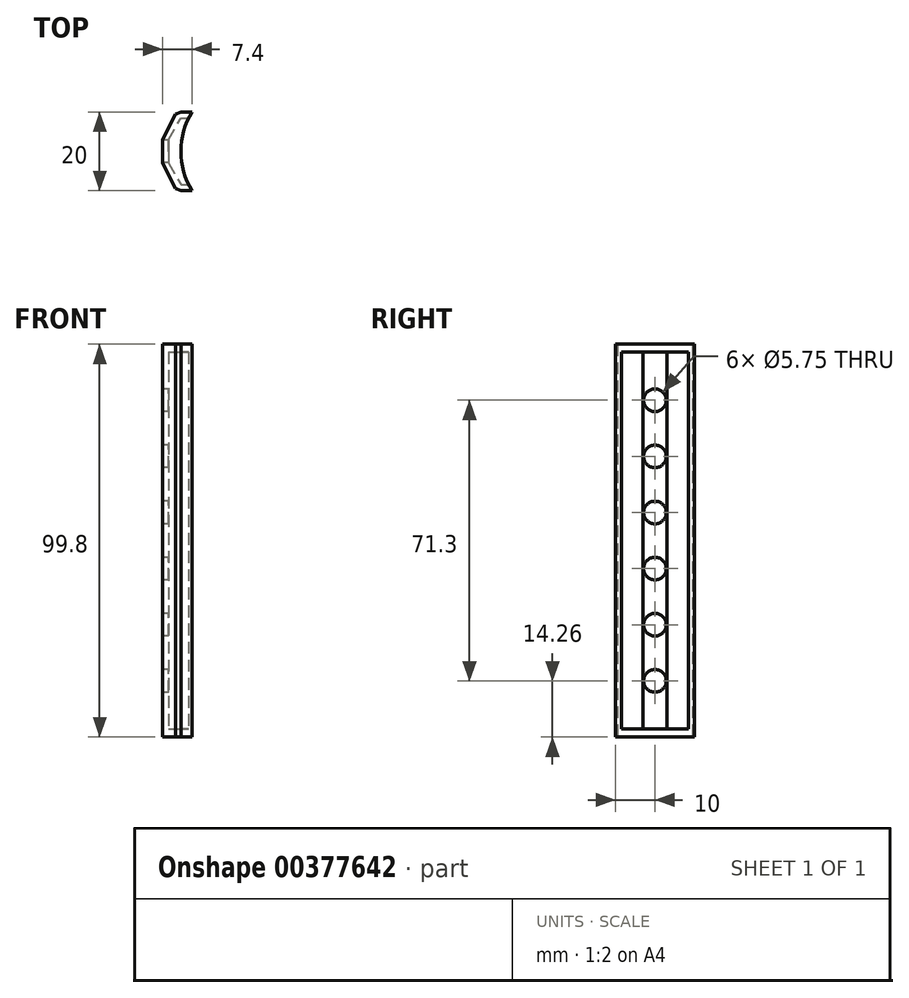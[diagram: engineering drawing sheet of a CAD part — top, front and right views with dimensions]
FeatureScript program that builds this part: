
annotation { "Feature Type Name" : "Feature", "Feature Type Description" : "" }
export const myFeature = defineFeature(function(context is Context, id is Id, definition is map)
    precondition{}
    {
        {
            var Q0;
            Q0=qCreatedBy(makeId("Top.planeOp"),FACE);
            var sketch = newSketch(context, id + "F0", { "sketchPlane" : qUnion([Q0])});
            skCircle(sketch, "E0", {"center": v(0, 0) * mm, "radius": 19.25 * mm});
            skLineSegment(sketch, "E1", {"start": v(-19.25, 0) * mm, "end": v(-22.35, 0) * mm, "construction": true});
            skLineSegment(sketch, "E2", {"start": v(-19.25, 0) * mm, "end": v(-19.25, 8.5) * mm, "construction": true});
            skLineSegment(sketch, "E3", {"start": v(-19.25, 0) * mm, "end": v(-19.25, -8.5) * mm, "construction": true});
            skLineSegment(sketch, "E4", {"start": v(-22.35, 0) * mm, "end": v(-22.35, 3) * mm});
            skLineSegment(sketch, "E5", {"start": v(-22.35, 0) * mm, "end": v(-22.35, -3) * mm});
            skLineSegment(sketch, "E6", {"start": v(-22.35, 3) * mm, "end": v(-19.25, 8.5) * mm});
            skLineSegment(sketch, "E7", {"start": v(-22.35, -3) * mm, "end": v(-19.25, -8.5) * mm});
            skLineSegment(sketch, "E8", {"start": v(-19.25, 8.5) * mm, "end": v(-17.27, 8.5) * mm});
            skLineSegment(sketch, "E9", {"start": v(-19.25, -8.5) * mm, "end": v(-17.27, -8.5) * mm});
            skLineSegment(sketch, "E10", {"start": v(-23.85, -3) * mm, "end": v(-23.85, 3) * mm});
            skLineSegment(sketch, "E11", {"start": v(-20.57, 9.5) * mm, "end": v(-23.85, 3) * mm});
            skLineSegment(sketch, "E12", {"start": v(-19.25, 10) * mm, "end": v(-16.45, 10) * mm});
            skLineSegment(sketch, "E13", {"start": v(-19.25, 10) * mm, "end": v(-20.57, 9.5) * mm});
            skLineSegment(sketch, "E14.MirrorCS", {"start": v(-19.25, -10) * mm, "end": v(-16.45, -10) * mm});
            skLineSegment(sketch, "E15.MirrorCS", {"start": v(-19.25, -10) * mm, "end": v(-20.57, -9.5) * mm});
            skLineSegment(sketch, "E16.MirrorCS", {"start": v(-20.57, -9.5) * mm, "end": v(-23.85, -3) * mm});
            skLineSegment(sketch, "E17", {"start": v(-16.45, 10) * mm, "end": v(-17.27, 8.5) * mm});
            skLineSegment(sketch, "E18", {"start": v(-17.27, -8.5) * mm, "end": v(-16.45, -10) * mm});
            skLineSegment(sketch, "E19", {"start": v(-23.85, -3) * mm, "end": v(-22.35, -3) * mm, "construction": true});
            skLineSegment(sketch, "E20", {"start": v(-23.85, 3) * mm, "end": v(-22.35, 3) * mm, "construction": true});
            skLineSegment(sketch, "E21", {"start": v(0, 0) * mm, "end": v(0, 19.25) * mm});
            skLineSegment(sketch, "E22", {"start": v(0, 0) * mm, "end": v(19.23, -0.79) * mm});
            skArc(sketch, "E23", {"start": v(-19.25, -1.74) * mm, "mid": v(-19.18, -2.37) * mm, "end": v(-19.1, -3) * mm});
            skSolve(sketch);
        }
        {
            var Q0;
            Q0=makeQuery(id+"F0.imprint","IMPRINT",FACE,{"disambiguationData":[TD([[makeQuery(id+"F0.imprint","IMPRINT",EDGE,{"derivedFrom":sQuery(id+"F0.wireOp",EDGE,"E4")}),1.0]])]});
            extrude(context, id + "F1", {"entities" : qUnion([Q0]), "depth" : 99.8 * mm});
        }
        {
            var Q0;
            Q0=makeQuery(id+"F1.opExtrude","SWEPT_FACE",FACE,{"disambiguationData":[OSD([sQuery(id+"F0.wireOp",EDGE,"E10")])]});
            var sketch = newSketch(context, id + "F2", { "sketchPlane" : qUnion([Q0])});
            skLineSegment(sketch, "E24", {"start": v(0, 0) * mm, "end": v(0, 99.8) * mm, "construction": true});
            skLineSegment(sketch, "E25", {"start": v(0, 0) * mm, "end": v(0, 14.26) * mm, "construction": true});
            skLineSegment(sketch, "E26", {"start": v(0, 14.26) * mm, "end": v(0, 28.52) * mm, "construction": true});
            skLineSegment(sketch, "E27", {"start": v(0, 28.52) * mm, "end": v(0, 42.78) * mm, "construction": true});
            skLineSegment(sketch, "E28", {"start": v(0, 42.78) * mm, "end": v(0, 57.04) * mm, "construction": true});
            skLineSegment(sketch, "E29", {"start": v(0, 57.04) * mm, "end": v(0, 71.3) * mm, "construction": true});
            skLineSegment(sketch, "E30", {"start": v(0, 71.3) * mm, "end": v(0, 85.56) * mm, "construction": true});
            skCircle(sketch, "E31", {"center": v(0, 14.26) * mm, "radius": 2.88 * mm});
            skCircle(sketch, "E32", {"center": v(0, 28.52) * mm, "radius": 2.88 * mm});
            skCircle(sketch, "E33", {"center": v(0, 42.78) * mm, "radius": 2.88 * mm});
            skCircle(sketch, "E34", {"center": v(0, 57.04) * mm, "radius": 2.88 * mm});
            skCircle(sketch, "E35", {"center": v(0, 71.3) * mm, "radius": 2.88 * mm});
            skCircle(sketch, "E36", {"center": v(0, 85.56) * mm, "radius": 2.88 * mm});
            skSolve(sketch);
        }
        {
            var Q0;
            Q0=makeQuery(id+"F2.imprint","IMPRINT",FACE,{"disambiguationData":[TD([[makeQuery(id+"F2.imprint","IMPRINT",EDGE,{"derivedFrom":sQuery(id+"F2.wireOp",EDGE,"E31")}),1.0]])]});
            var Q1;
            Q1=makeQuery(id+"F2.imprint","IMPRINT",FACE,{"disambiguationData":[TD([[makeQuery(id+"F2.imprint","IMPRINT",EDGE,{"derivedFrom":sQuery(id+"F2.wireOp",EDGE,"E32")}),1.0]])]});
            var Q2;
            Q2=makeQuery(id+"F2.imprint","IMPRINT",FACE,{"disambiguationData":[TD([[makeQuery(id+"F2.imprint","IMPRINT",EDGE,{"derivedFrom":sQuery(id+"F2.wireOp",EDGE,"E33")}),1.0]])]});
            var Q3;
            Q3=makeQuery(id+"F2.imprint","IMPRINT",FACE,{"disambiguationData":[TD([[makeQuery(id+"F2.imprint","IMPRINT",EDGE,{"derivedFrom":sQuery(id+"F2.wireOp",EDGE,"E34")}),1.0]])]});
            var Q4;
            Q4=makeQuery(id+"F2.imprint","IMPRINT",FACE,{"disambiguationData":[TD([[makeQuery(id+"F2.imprint","IMPRINT",EDGE,{"derivedFrom":sQuery(id+"F2.wireOp",EDGE,"E35")}),1.0]])]});
            var Q5;
            Q5=makeQuery(id+"F2.imprint","IMPRINT",FACE,{"disambiguationData":[TD([[makeQuery(id+"F2.imprint","IMPRINT",EDGE,{"derivedFrom":sQuery(id+"F2.wireOp",EDGE,"E36")}),1.0]])]});
            extrude(context, id + "F3", {"entities" : qUnion([Q0, Q1, Q2, Q3, Q4, Q5]), "operationType" : NewBodyOperationType.REMOVE, "oppositeDirection" : true, "depth" : 4 * mm});
        }
        {
            var Q0;
            Q0=makeQuery(id+"F0.imprint","IMPRINT",FACE,{"disambiguationData":[TD([[makeQuery(id+"F0.imprint","IMPRINT",EDGE,{"derivedFrom":sQuery(id+"F0.wireOp",EDGE,"E4")}),-1.0]])]});
            extrude(context, id + "F4", {"entities" : qUnion([Q0]), "operationType" : NewBodyOperationType.ADD, "depth" : 2 * mm});
        }
        {
            var Q0;
            Q0=makeQuery(id+"F1.opExtrude","CAP_FACE",FACE,{"disambiguationData":[OSD([sQuery(id+"F0.wireOp",EDGE,"E0"),sQuery(id+"F0.wireOp",EDGE,"E4"),sQuery(id+"F0.wireOp",EDGE,"E5"),sQuery(id+"F0.wireOp",EDGE,"E6"),sQuery(id+"F0.wireOp",EDGE,"E7"),sQuery(id+"F0.wireOp",EDGE,"E8"),sQuery(id+"F0.wireOp",EDGE,"E9"),sQuery(id+"F0.wireOp",EDGE,"E10"),sQuery(id+"F0.wireOp",EDGE,"E11"),sQuery(id+"F0.wireOp",EDGE,"E12"),sQuery(id+"F0.wireOp",EDGE,"E13"),sQuery(id+"F0.wireOp",EDGE,"E14.MirrorCS"),sQuery(id+"F0.wireOp",EDGE,"E15.MirrorCS"),sQuery(id+"F0.wireOp",EDGE,"E16.MirrorCS")])],"isStart":false});
            var sketch = newSketch(context, id + "F5", { "sketchPlane" : qUnion([Q0])});
            skCircle(sketch, "E37", {"center": v(0, 0) * mm, "radius": 19.25 * mm});
            skSolve(sketch);
        }
        {
            var Q0;
            Q0=makeQuery(id+"F5.imprint","IMPRINT",FACE,{"disambiguationData":[TD([[makeQuery(id+"F5.imprint","IMPRINT",EDGE,{"derivedFrom":makeQuery(id+"F1.opExtrude","CAP_EDGE",EDGE,{"disambiguationData":[OSD([sQuery(id+"F0.wireOp",EDGE,"E6")])],"isStart":false})}),-1.0]])]});
            extrude(context, id + "F6", {"entities" : qUnion([Q0]), "operationType" : NewBodyOperationType.ADD, "oppositeDirection" : true, "depth" : 2 * mm});
        }
    });
